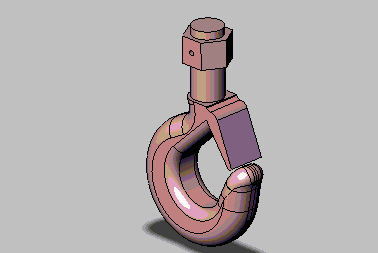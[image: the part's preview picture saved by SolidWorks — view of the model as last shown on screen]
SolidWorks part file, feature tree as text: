
SOLIDWORKS PART (.sldprt)
format: sldprt  version: not decoded by parser v0  size: 1,524,224 bytes
history: native  units: mm
features: plane x5, sketch x4, extrude x3, fillet x2, material x1, mirror x1, cut_extrude x1 (+10 scaffold rows collapsed)
feature tree (27):
  scaffold x10  (default folders/planes/origin — collapsed)
  material  "Material <not specified>"
  plane  "Plane1"  Offset=0mm
  plane  "Plane2"  Offset=0mm
  plane  "Plane3"  Offset=0mm
  sketch  "Sketch1"
  extrude  "Extrude1"  Depth=17.4625mm
  fillet  "Fillet1"  Radius=15.08125mm
  fillet  "Fillet2"  Radius=8.73125mm
  mirror  "Mirror1"
  sketch  "Sketch2"  dims[D1=28.575mm]
  extrude  "Extrude2"  Depth=63.5mm
  plane  "Plane4"  Offset=0mm
  plane  "Plane5"  Offset=31.75mm
  sketch  "Sketch3"  dims[D1=~37.30625mm D2=~37.30625mm]
  extrude  "Extrude3"  Depth=24.60625mm
  sketch  "Sketch4"  dims[D1=4.7625mm D2=~12.303125mm]
  cut_extrude  "Cut-Extrude1"  [1 undecoded]
decode coverage: 8 of 11 modeling features carry decoded parameters
note: ~ marks probable driven/reference dimensions
note: 1 parameter value undecoded
note: suppression state not decoded; provenance and decode notes live in map.json
